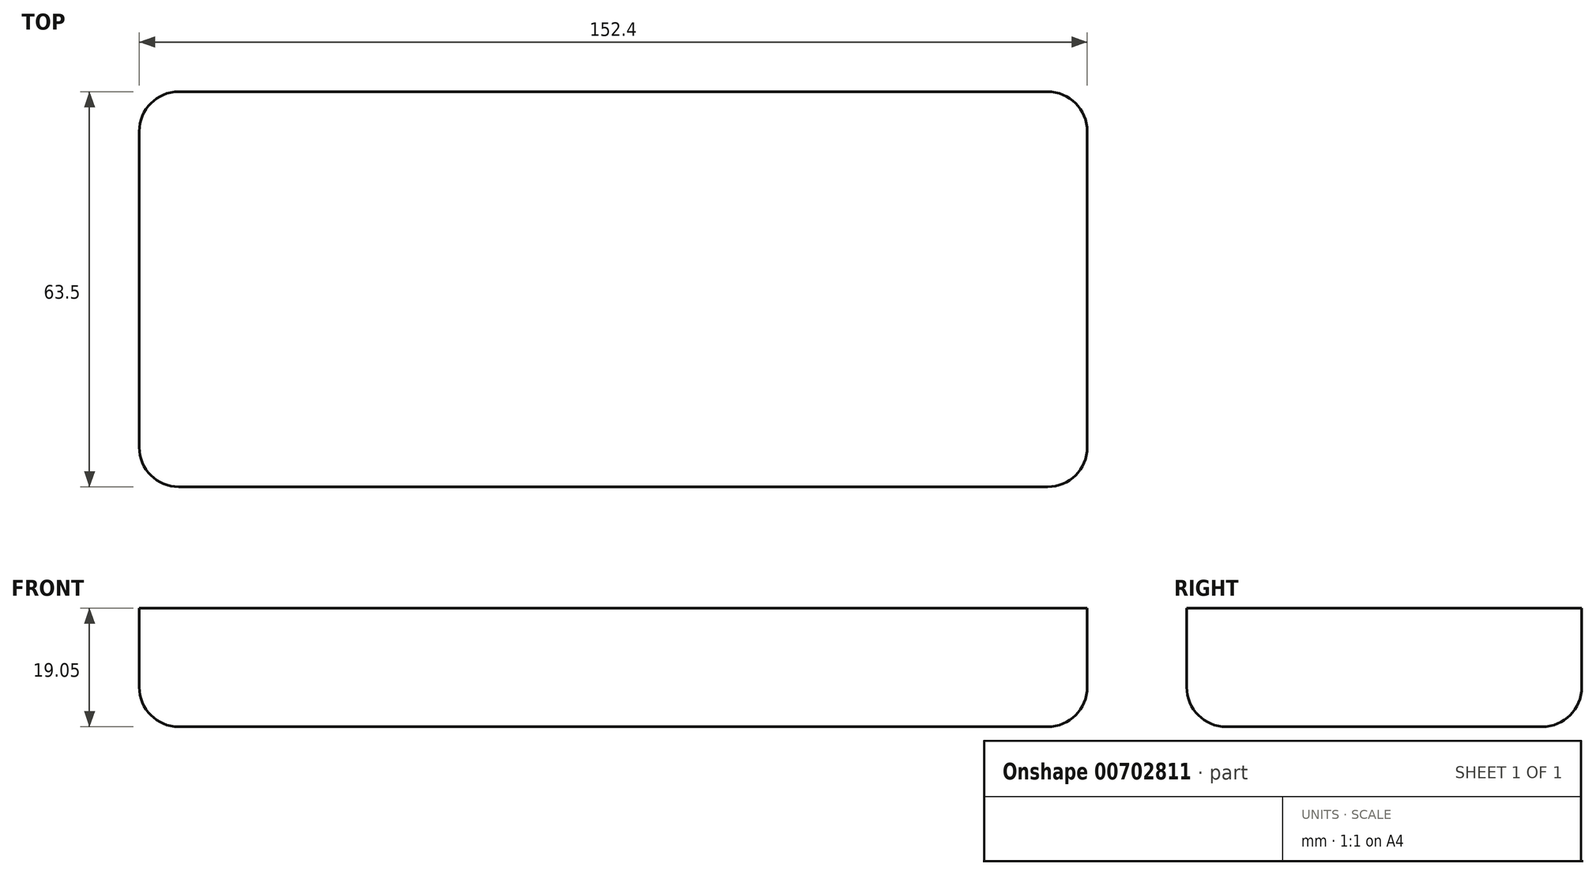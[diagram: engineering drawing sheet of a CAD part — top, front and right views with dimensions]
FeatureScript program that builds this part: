
annotation { "Feature Type Name" : "Feature", "Feature Type Description" : "" }
export const myFeature = defineFeature(function(context is Context, id is Id, definition is map)
    precondition{}
    {
        {
            var Q0;
            Q0=qCreatedBy(makeId("Top.planeOp"),FACE);
            var sketch = newSketch(context, id + "F0", { "sketchPlane" : qUnion([Q0])});
            skLineSegment(sketch, "E0.bottom", {"start": v(-76.2, -31.75) * mm, "end": v(76.2, -31.75) * mm});
            skLineSegment(sketch, "E0.top", {"start": v(-76.2, 31.75) * mm, "end": v(76.2, 31.75) * mm});
            skLineSegment(sketch, "E0.left", {"start": v(-76.2, -31.75) * mm, "end": v(-76.2, 31.75) * mm});
            skLineSegment(sketch, "E0.right", {"start": v(76.2, -31.75) * mm, "end": v(76.2, 31.75) * mm});
            skPoint(sketch, "E0.middle", {"position": v(0, 0) * mm});
            skSolve(sketch);
        }
        {
            var Q0;
            Q0=makeQuery(id+"F0.imprint","IMPRINT",FACE,{"disambiguationData":[TD([[makeQuery(id+"F0.imprint","IMPRINT",EDGE,{"derivedFrom":sQuery(id+"F0.wireOp",EDGE,"E0.bottom")}),1.0]])]});
            extrude(context, id + "F1", {"entities" : qUnion([Q0]), "depth" : 38.1 * mm, "offsetDistance" : 25.4 * mm});
        }
        {
            var Q0;
            Q0=makeQuery(id+"F1.opExtrude","CAP_FACE",FACE,{"disambiguationData":[OSD([sQuery(id+"F0.wireOp",EDGE,"E0.bottom"),sQuery(id+"F0.wireOp",EDGE,"E0.top"),sQuery(id+"F0.wireOp",EDGE,"E0.left"),sQuery(id+"F0.wireOp",EDGE,"E0.right")])],"isStart":false});
            var Q1;
            Q1=makeQuery(id+"F1.opExtrude","CAP_FACE",FACE,{"disambiguationData":[OSD([sQuery(id+"F0.wireOp",EDGE,"E0.bottom"),sQuery(id+"F0.wireOp",EDGE,"E0.top"),sQuery(id+"F0.wireOp",EDGE,"E0.left"),sQuery(id+"F0.wireOp",EDGE,"E0.right")])],"isStart":true});
            var Q2;
            Q2=makeQuery(id+"F1.opExtrude","SWEPT_FACE",FACE,{"disambiguationData":[OSD([sQuery(id+"F0.wireOp",EDGE,"E0.left")])]});
            var Q3;
            Q3=makeQuery(id+"F1.opExtrude","SWEPT_FACE",FACE,{"disambiguationData":[OSD([sQuery(id+"F0.wireOp",EDGE,"E0.bottom")])]});
            var Q4;
            Q4=makeQuery(id+"F1.opExtrude","SWEPT_FACE",FACE,{"disambiguationData":[OSD([sQuery(id+"F0.wireOp",EDGE,"E0.top")])]});
            var Q5;
            Q5=makeQuery(id+"F1.opExtrude","SWEPT_FACE",FACE,{"disambiguationData":[OSD([sQuery(id+"F0.wireOp",EDGE,"E0.right")])]});
            fillet(context, id + "F2", {"entities" : qUnion([Q0, Q1, Q2, Q3, Q4, Q5]), "radius" : 6.35 * mm, "tangentPropagation" : true, "allowEdgeOverflow" : false});
        }
        {
            var Q0;
            Q0=qCreatedBy(makeId("Top.planeOp"),FACE);
            var sketch = newSketch(context, id + "F3", { "sketchPlane" : qUnion([Q0])});
            skLineSegment(sketch, "E1.bottom", {"start": v(-90.65, 39.95) * mm, "end": v(92.54, 39.95) * mm});
            skLineSegment(sketch, "E1.top", {"start": v(-90.65, -43.73) * mm, "end": v(92.54, -43.73) * mm});
            skLineSegment(sketch, "E1.left", {"start": v(-90.65, 39.95) * mm, "end": v(-90.65, -43.73) * mm});
            skLineSegment(sketch, "E1.right", {"start": v(92.54, 39.95) * mm, "end": v(92.54, -43.73) * mm});
            skSolve(sketch);
        }
        {
            var Q0;
            Q0 = qSketchRegion(id + "F3", true);
            extrude(context, id + "F4", {"entities" : qUnion([Q0]), "operationType" : NewBodyOperationType.INTERSECT, "depth" : 19.05 * mm, "offsetDistance" : 25.4 * mm});
        }
    });
